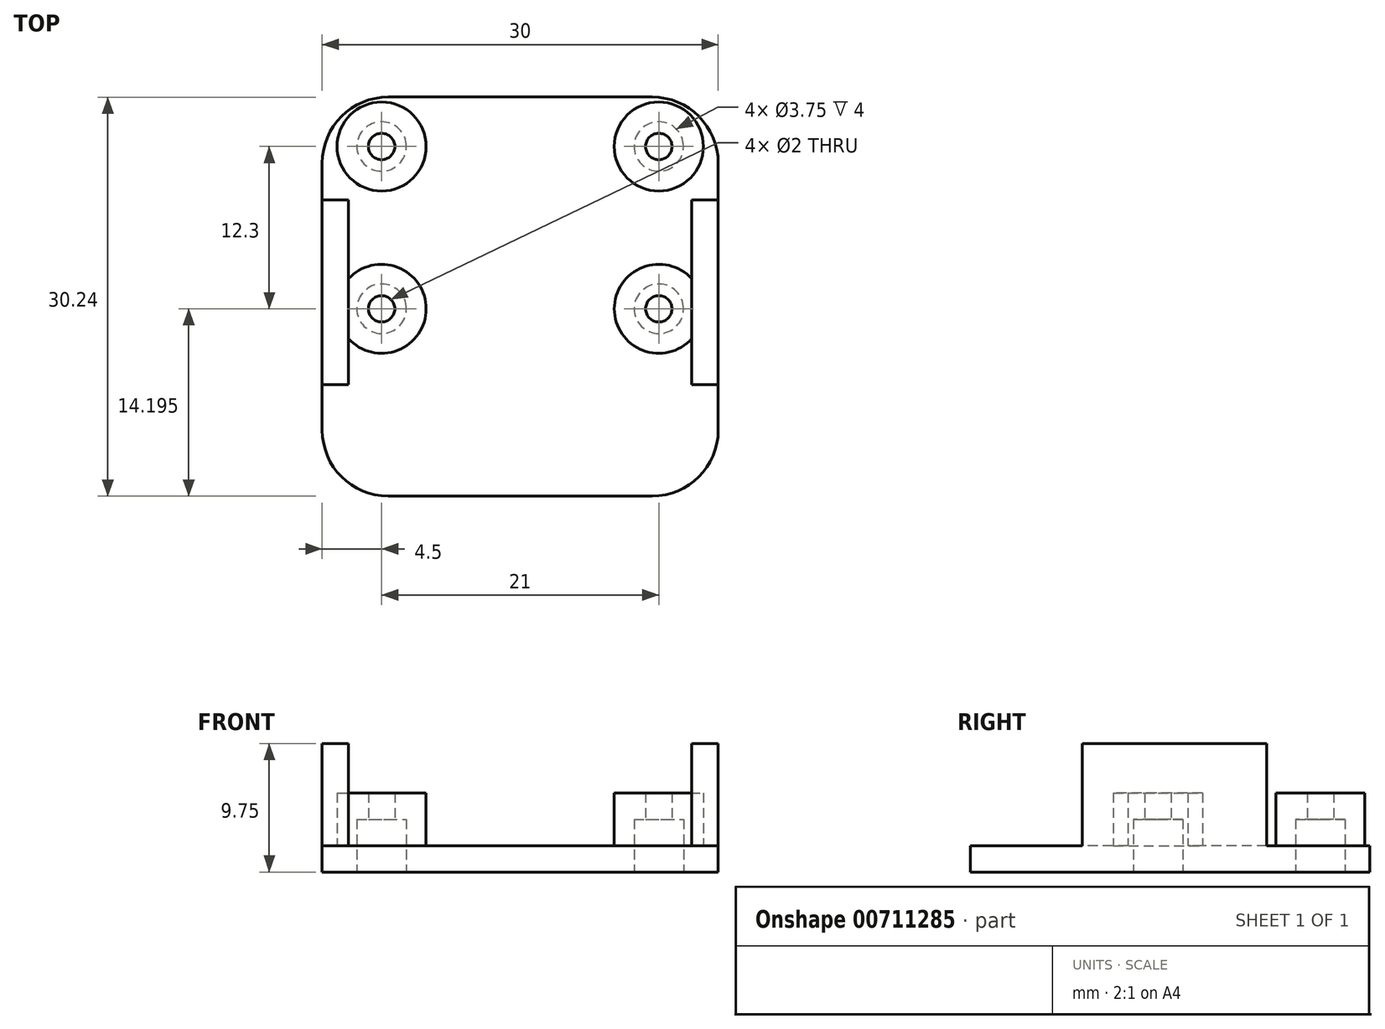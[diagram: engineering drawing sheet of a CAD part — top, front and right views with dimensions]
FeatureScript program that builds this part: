
annotation { "Feature Type Name" : "Feature", "Feature Type Description" : "" }
export const myFeature = defineFeature(function(context is Context, id is Id, definition is map)
    precondition{}
    {
        {
            var Q0;
            Q0=qCreatedBy(makeId("Top.planeOp"),FACE);
            var sketch = newSketch(context, id + "F0", { "sketchPlane" : qUnion([Q0])});
            skLineSegment(sketch, "E0.bottom", {"start": v(15, 15.13) * mm, "end": v(-15, 15.13) * mm});
            skLineSegment(sketch, "E0.top", {"start": v(15, -15.12) * mm, "end": v(-15, -15.12) * mm});
            skLineSegment(sketch, "E0.left", {"start": v(15, 15.13) * mm, "end": v(15, -15.13) * mm});
            skLineSegment(sketch, "E0.right", {"start": v(-15, 15.13) * mm, "end": v(-15, -15.12) * mm});
            skPoint(sketch, "E0.middle", {"position": v(0, 0) * mm});
            skSolve(sketch);
        }
        {
            var Q0;
            Q0=makeQuery(id+"F0.imprint","IMPRINT",FACE,{"disambiguationData":[TD([[makeQuery(id+"F0.imprint","IMPRINT",EDGE,{"derivedFrom":sQuery(id+"F0.wireOp",EDGE,"E0.bottom")}),1.0]])]});
            extrude(context, id + "F1", {"entities" : qUnion([Q0]), "depth" : 2 * mm, "offsetDistance" : 25 * mm});
        }
        {
            var Q0;
            Q0=makeQuery(id+"F1.opExtrude","CAP_FACE",FACE,{"disambiguationData":[OSD([sQuery(id+"F0.wireOp",EDGE,"E0.bottom"),sQuery(id+"F0.wireOp",EDGE,"E0.top"),sQuery(id+"F0.wireOp",EDGE,"E0.left"),sQuery(id+"F0.wireOp",EDGE,"E0.right")])],"isStart":false});
            var sketch = newSketch(context, id + "F2", { "sketchPlane" : qUnion([Q0])});
            skPoint(sketch, "E1.0", {"position": v(-15, 15.13) * mm});
            skPoint(sketch, "E2.0", {"position": v(-15, -15.12) * mm});
            skLineSegment(sketch, "E3.0", {"start": v(-15, 15.13) * mm, "end": v(-15, -15.12) * mm});
            skLineSegment(sketch, "E4.bottom", {"start": v(-15, 7.33) * mm, "end": v(-13, 7.33) * mm});
            skLineSegment(sketch, "E4.top", {"start": v(-15, -6.68) * mm, "end": v(-13, -6.68) * mm});
            skLineSegment(sketch, "E4.left", {"start": v(-15, 7.33) * mm, "end": v(-15, -6.68) * mm});
            skLineSegment(sketch, "E4.right", {"start": v(-13, 7.33) * mm, "end": v(-13, -6.68) * mm});
            skLineSegment(sketch, "E5", {"start": v(0, 8.18) * mm, "end": v(0, -9.57) * mm, "construction": true});
            skLineSegment(sketch, "E6.MirrorCS", {"start": v(15, 7.33) * mm, "end": v(13, 7.33) * mm});
            skLineSegment(sketch, "E7.MirrorCS", {"start": v(15, -6.68) * mm, "end": v(13, -6.68) * mm});
            skLineSegment(sketch, "E8.MirrorCS", {"start": v(15, 7.33) * mm, "end": v(15, -6.68) * mm});
            skLineSegment(sketch, "E9.MirrorCS", {"start": v(13, 7.33) * mm, "end": v(13, -6.68) * mm});
            skSolve(sketch);
        }
        {
            var Q0;
            Q0=makeQuery(id+"F2.imprint","IMPRINT",FACE,{"disambiguationData":[TD([[makeQuery(id+"F2.imprint","IMPRINT",EDGE,{"derivedFrom":sQuery(id+"F2.wireOp",EDGE,"E4.bottom")}),-1.0]])]});
            var Q1;
            Q1=makeQuery(id+"F2.imprint","IMPRINT",FACE,{"disambiguationData":[TD([[makeQuery(id+"F2.imprint","IMPRINT",EDGE,{"derivedFrom":sQuery(id+"F2.wireOp",EDGE,"E6.MirrorCS")}),1.0]])]});
            extrude(context, id + "F3", {"entities" : qUnion([Q0, Q1]), "operationType" : NewBodyOperationType.ADD, "depth" : 7.75 * mm, "offsetDistance" : 25 * mm});
        }
        {
            var Q0;
            Q0=makeQuery(id+"F1.opExtrude","CAP_FACE",FACE,{"disambiguationData":[OSD([sQuery(id+"F0.wireOp",EDGE,"E0.bottom"),sQuery(id+"F0.wireOp",EDGE,"E0.top"),sQuery(id+"F0.wireOp",EDGE,"E0.left"),sQuery(id+"F0.wireOp",EDGE,"E0.right")])],"isStart":true});
            var sketch = newSketch(context, id + "F4", { "sketchPlane" : qUnion([Q0])});
            skCircle(sketch, "E10", {"center": v(-10.5, -11.38) * mm, "radius": 1.88 * mm});
            skLineSegment(sketch, "E11", {"start": v(0, -15.13) * mm, "end": v(0, 15.12) * mm, "construction": true});
            skCircle(sketch, "E12.0.1.0", {"center": v(-10.5, 0.92) * mm, "radius": 1.88 * mm});
            skCircle(sketch, "E12.1.0.0", {"center": v(10.5, -11.38) * mm, "radius": 1.88 * mm});
            skCircle(sketch, "E12.1.1.0", {"center": v(10.5, 0.92) * mm, "radius": 1.88 * mm});
            skLineSegment(sketch, "E12.direction1", {"start": v(-10.5, -11.38) * mm, "end": v(10.5, -11.38) * mm, "construction": true});
            skLineSegment(sketch, "E12.direction2", {"start": v(-10.5, -11.38) * mm, "end": v(-10.5, 0.92) * mm, "construction": true});
            skPoint(sketch, "E13", {"position": v(0, -11.38) * mm});
            skSolve(sketch);
        }
        {
            var Q0;
            Q0=makeQuery(id+"F4.imprint","IMPRINT",FACE,{"disambiguationData":[TD([[makeQuery(id+"F4.imprint","IMPRINT",EDGE,{"derivedFrom":sQuery(id+"F4.wireOp",EDGE,"E10")}),-1.0]])]});
            var sketch = newSketch(context, id + "F5", { "sketchPlane" : qUnion([Q0])});
            skCircle(sketch, "E14.0", {"center": v(10.5, -11.38) * mm, "radius": 3.38 * mm});
            skCircle(sketch, "E15.0", {"center": v(-10.5, -11.38) * mm, "radius": 3.38 * mm});
            skCircle(sketch, "E16.0", {"center": v(-10.5, 0.92) * mm, "radius": 3.38 * mm});
            skCircle(sketch, "E17.0", {"center": v(10.5, 0.92) * mm, "radius": 3.38 * mm});
            skSolve(sketch);
        }
        {
            var Q0;
            Q0 = qSketchRegion(id + "F5", true);
            extrude(context, id + "F6", {"entities" : qUnion([Q0]), "operationType" : NewBodyOperationType.ADD, "oppositeDirection" : true, "depth" : 6 * mm, "offsetDistance" : 25 * mm});
        }
        {
            var Q0;
            Q0 = qSketchRegion(id + "F4", true);
            extrude(context, id + "F7", {"entities" : qUnion([Q0]), "operationType" : NewBodyOperationType.REMOVE, "oppositeDirection" : true, "depth" : 4 * mm, "offsetDistance" : 25 * mm});
        }
        {
            var Q0;
            Q0=makeQuery(id+"F1.opExtrude","CAP_FACE",FACE,{"disambiguationData":[OSD([sQuery(id+"F0.wireOp",EDGE,"E0.bottom"),sQuery(id+"F0.wireOp",EDGE,"E0.top"),sQuery(id+"F0.wireOp",EDGE,"E0.left"),sQuery(id+"F0.wireOp",EDGE,"E0.right")])],"isStart":true});
            var sketch = newSketch(context, id + "F8", { "sketchPlane" : qUnion([Q0])});
            skPoint(sketch, "E18", {"position": v(-10.5, 0.92) * mm});
            skPoint(sketch, "E19", {"position": v(-10.5, -11.38) * mm});
            skPoint(sketch, "E20", {"position": v(10.5, -11.38) * mm});
            skPoint(sketch, "E21", {"position": v(10.5, 0.92) * mm});
            skSolve(sketch);
        }
        {
            var Q0;
            Q0=sQuery(id+"F8.wireOp",VERTEX,"E18");
            var Q1;
            Q1=sQuery(id+"F8.wireOp",VERTEX,"E19");
            var Q2;
            Q2=sQuery(id+"F8.wireOp",VERTEX,"E20");
            var Q3;
            Q3=sQuery(id+"F8.wireOp",VERTEX,"E21");
            var Q4;
            Q4=makeQuery(id+"F1.opExtrude","SWEPT_BODY",BODY,{"disambiguationData":[OSD([sQuery(id+"F0.wireOp",EDGE,"E0.bottom"),sQuery(id+"F0.wireOp",EDGE,"E0.top"),sQuery(id+"F0.wireOp",EDGE,"E0.left"),sQuery(id+"F0.wireOp",EDGE,"E0.right")])]});
            hole(context, id + "F9", {"style" : HoleStyle.SIMPLE, "endStyle" : HoleEndStyle.BLIND, "holeDiameter" : 2 * mm, "majorDiameter" : 5 * mm, "holeDepth" : 4 * mm, "isTappedThrough" : true, "tappedDepth" : 12 * mm, "tapClearance" : 3, "locations" : qUnion([Q0, Q1, Q2, Q3]), "scope" : qUnion([Q4])});
        }
        {
            var Q0;
            Q0=makeQuery(id+"F1.opExtrude","SWEPT_EDGE",EDGE,{"disambiguationData":[OSD([sQuery(id+"F0.wireOp",EDGE,"E0.top"),sQuery(id+"F0.wireOp",EDGE,"E0.right")])]});
            var Q1;
            Q1=makeQuery(id+"F1.opExtrude","SWEPT_EDGE",EDGE,{"disambiguationData":[OSD([sQuery(id+"F0.wireOp",EDGE,"E0.top"),sQuery(id+"F0.wireOp",EDGE,"E0.left")])]});
            var Q2;
            Q2=makeQuery(id+"F1.opExtrude","SWEPT_EDGE",EDGE,{"disambiguationData":[OSD([sQuery(id+"F0.wireOp",EDGE,"E0.bottom"),sQuery(id+"F0.wireOp",EDGE,"E0.left")])]});
            var Q3;
            Q3=makeQuery(id+"F1.opExtrude","SWEPT_EDGE",EDGE,{"disambiguationData":[OSD([sQuery(id+"F0.wireOp",EDGE,"E0.bottom"),sQuery(id+"F0.wireOp",EDGE,"E0.right")])]});
            fillet(context, id + "F10", {"entities" : qUnion([Q0, Q1, Q2, Q3]), "radius" : 5 * mm, "tangentPropagation" : true, "allowEdgeOverflow" : false});
        }
    });
